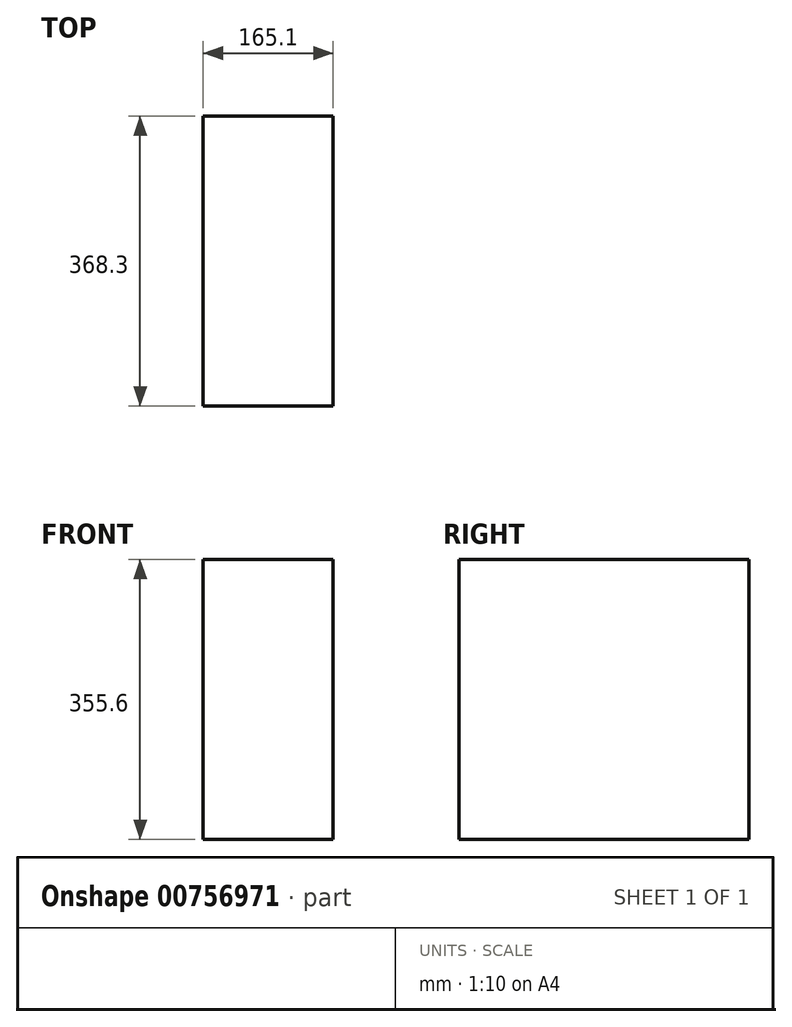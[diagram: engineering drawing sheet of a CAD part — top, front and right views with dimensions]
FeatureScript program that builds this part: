
annotation { "Feature Type Name" : "Feature", "Feature Type Description" : "" }
export const myFeature = defineFeature(function(context is Context, id is Id, definition is map)
    precondition{}
    {
        {
            var Q0;
            Q0=qCreatedBy(makeId("Front.planeOp"),FACE);
            var sketch = newSketch(context, id + "F0", { "sketchPlane" : qUnion([Q0])});
            skLineSegment(sketch, "E0.bottom", {"start": v(82.55, 177.8) * mm, "end": v(-82.55, 177.8) * mm});
            skLineSegment(sketch, "E0.top", {"start": v(82.55, -177.8) * mm, "end": v(-82.55, -177.8) * mm});
            skLineSegment(sketch, "E0.left", {"start": v(82.55, 177.8) * mm, "end": v(82.55, -177.8) * mm});
            skLineSegment(sketch, "E0.right", {"start": v(-82.55, 177.8) * mm, "end": v(-82.55, -177.8) * mm});
            skPoint(sketch, "E0.middle", {"position": v(0, 0) * mm});
            skSolve(sketch);
        }
        {
            var Q0;
            Q0=qSketchRegion(id+"F0",true);
            extrude(context, id + "F1", {"entities" : qUnion([Q0]), "endBound" : BoundingType.SYMMETRIC, "depth" : 368.3 * mm});
        }
    });
